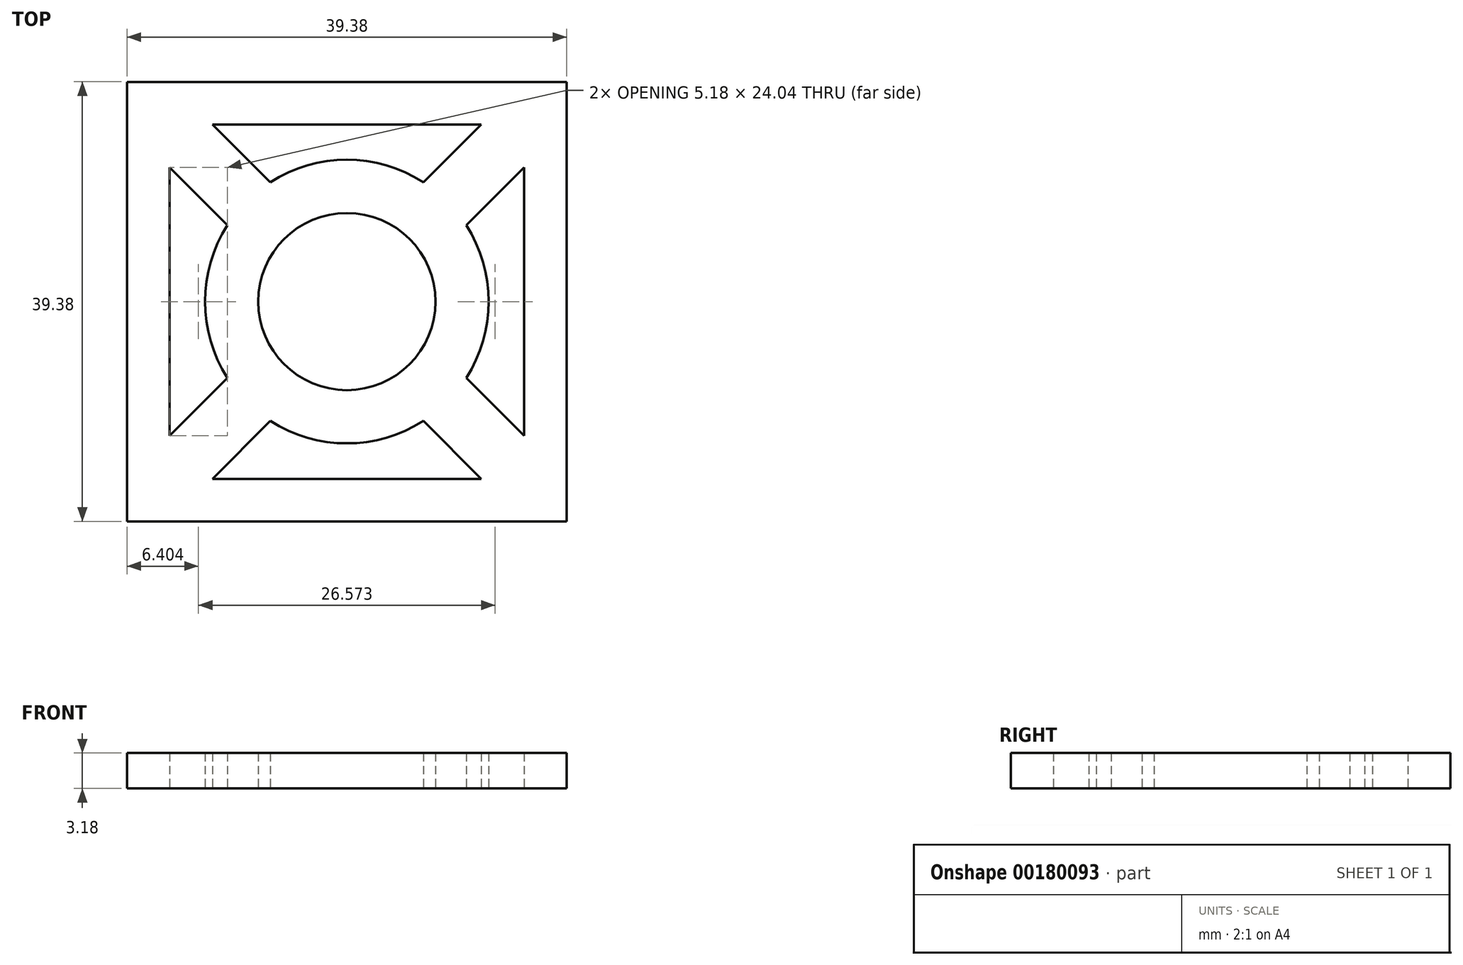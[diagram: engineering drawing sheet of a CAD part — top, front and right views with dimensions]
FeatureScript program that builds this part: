
annotation { "Feature Type Name" : "Feature", "Feature Type Description" : "" }
export const myFeature = defineFeature(function(context is Context, id is Id, definition is map)
    precondition{}
    {
        {
            var Q0;
            Q0=qCreatedBy(makeId("Top.planeOp"),FACE);
            var sketch = newSketch(context, id + "F0", { "sketchPlane" : qUnion([Q0])});
            skLineSegment(sketch, "E0", {"start": v(0, -19.24) * mm, "end": v(0, 22.54) * mm, "construction": true});
            skLineSegment(sketch, "E1", {"start": v(-20.81, 0) * mm, "end": v(25.14, 0) * mm, "construction": true});
            skArc(sketch, "E2", {"start": v(-10.7, 6.84) * mm, "mid": v(-12.7, 0) * mm, "end": v(-10.7, -6.84) * mm});
            skLineSegment(sketch, "E3.0", {"start": v(-12.02, 15.88) * mm, "end": v(12.02, 15.88) * mm});
            skLineSegment(sketch, "E3.1", {"start": v(-15.88, 12.02) * mm, "end": v(-15.88, -12.02) * mm});
            skLineSegment(sketch, "E3.2", {"start": v(-12.02, -15.88) * mm, "end": v(12.02, -15.88) * mm});
            skLineSegment(sketch, "E3.3", {"start": v(15.88, 12.02) * mm, "end": v(15.88, -12.02) * mm});
            skCircle(sketch, "E4", {"center": v(0, 0) * mm, "radius": 7.94 * mm});
            skLineSegment(sketch, "E5", {"start": v(-15.88, -15.88) * mm, "end": v(15.88, 15.88) * mm, "construction": true});
            skLineSegment(sketch, "E6", {"start": v(15.88, -15.88) * mm, "end": v(-15.88, 15.88) * mm, "construction": true});
            skLineSegment(sketch, "E7", {"start": v(-15.88, 12.02) * mm, "end": v(-10.7, 6.84) * mm});
            skLineSegment(sketch, "E8.MirrorCS", {"start": v(-12.02, 15.88) * mm, "end": v(-6.84, 10.7) * mm});
            skLineSegment(sketch, "E9.MirrorCS", {"start": v(15.88, -12.02) * mm, "end": v(10.7, -6.84) * mm});
            skLineSegment(sketch, "E10.MirrorCS", {"start": v(12.02, -15.88) * mm, "end": v(6.84, -10.7) * mm});
            skLineSegment(sketch, "E11.MirrorCS", {"start": v(15.88, 12.02) * mm, "end": v(10.7, 6.84) * mm});
            skLineSegment(sketch, "E12.MirrorCS", {"start": v(12.02, 15.88) * mm, "end": v(6.84, 10.7) * mm});
            skLineSegment(sketch, "E13.MirrorCS", {"start": v(-12.02, -15.88) * mm, "end": v(-6.84, -10.7) * mm});
            skLineSegment(sketch, "E14.MirrorCS", {"start": v(-15.88, -12.02) * mm, "end": v(-10.7, -6.84) * mm});
            skLineSegment(sketch, "E15.0", {"start": v(-19.69, 19.69) * mm, "end": v(19.69, 19.69) * mm});
            skLineSegment(sketch, "E15.1", {"start": v(-19.69, 19.69) * mm, "end": v(-19.69, -19.69) * mm});
            skLineSegment(sketch, "E15.2", {"start": v(-19.69, -19.69) * mm, "end": v(19.69, -19.69) * mm});
            skLineSegment(sketch, "E15.3", {"start": v(19.69, 19.69) * mm, "end": v(19.69, -19.69) * mm});
            skArc(sketch, "E16.trimOffspring", {"start": v(6.84, 10.7) * mm, "mid": v(0, 12.7) * mm, "end": v(-6.84, 10.7) * mm});
            skArc(sketch, "E17.trimOffspring", {"start": v(10.7, -6.84) * mm, "mid": v(12.7, 0) * mm, "end": v(10.7, 6.84) * mm});
            skArc(sketch, "E18.trimOffspring", {"start": v(-6.84, -10.7) * mm, "mid": v(0, -12.7) * mm, "end": v(6.84, -10.7) * mm});
            skSolve(sketch);
        }
        {
            var Q0;
            Q0=makeQuery(id+"F0.imprint","IMPRINT",FACE,{"disambiguationData":[TD([[makeQuery(id+"F0.imprint","IMPRINT",EDGE,{"derivedFrom":sQuery(id+"F0.wireOp",EDGE,"E2")}),1.0]])]});
            extrude(context, id + "F1", {"entities" : qUnion([Q0]), "depth" : 3.17 * mm});
        }
    });
